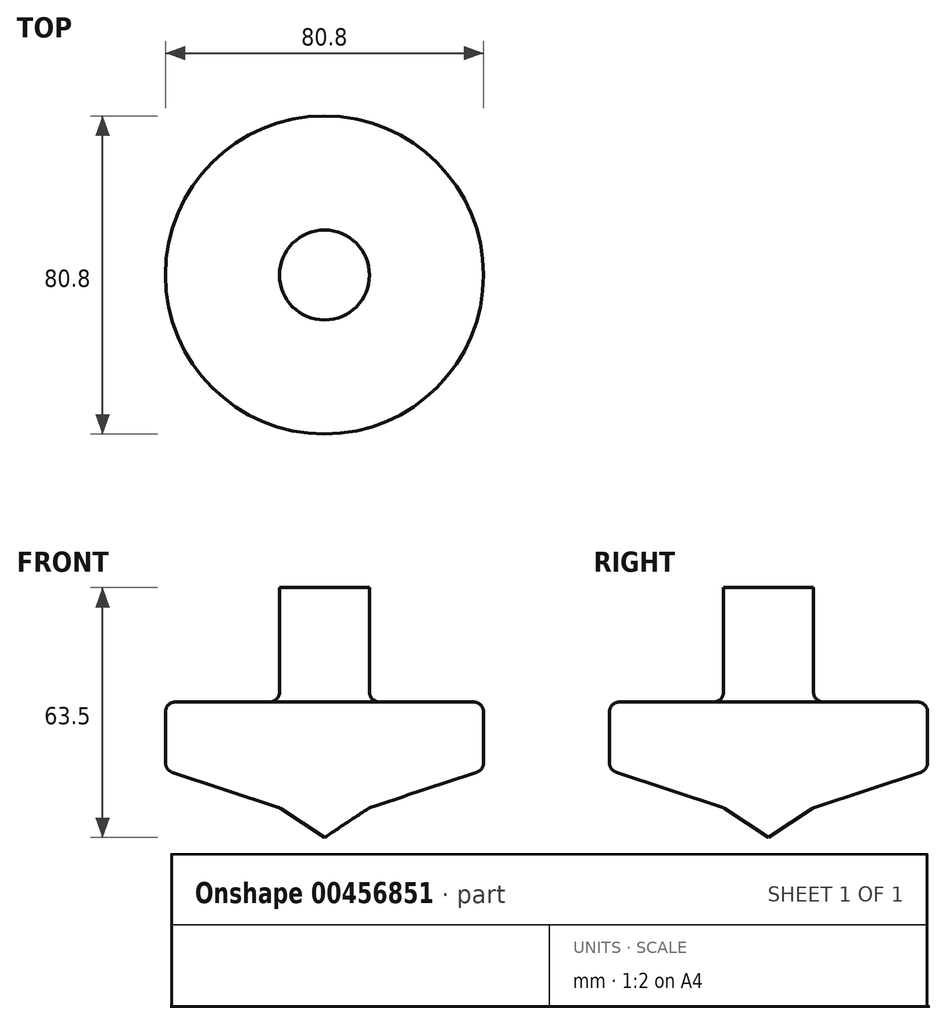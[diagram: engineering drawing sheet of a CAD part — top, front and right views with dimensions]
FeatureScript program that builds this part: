
annotation { "Feature Type Name" : "Feature", "Feature Type Description" : "" }
export const myFeature = defineFeature(function(context is Context, id is Id, definition is map)
    precondition{}
    {
        {
            var Q0;
            Q0=qCreatedBy(makeId("Front.planeOp"),FACE);
            var sketch = newSketch(context, id + "F0", { "sketchPlane" : qUnion([Q0])});
            skLineSegment(sketch, "E0", {"start": v(40.4, 18.98) * mm, "end": v(40.4, 31.89) * mm});
            skLineSegment(sketch, "E1", {"start": v(37.86, 34.43) * mm, "end": v(13.97, 34.43) * mm});
            skLineSegment(sketch, "E2", {"start": v(11.43, 36.97) * mm, "end": v(11.43, 63.5) * mm});
            skLineSegment(sketch, "E3", {"start": v(11.43, 63.5) * mm, "end": v(0, 63.5) * mm});
            skLineSegment(sketch, "E4", {"start": v(0, 0) * mm, "end": v(11.15, 7.37) * mm});
            skLineSegment(sketch, "E5", {"start": v(11.75, 7.67) * mm, "end": v(38.66, 16.57) * mm});
            skPoint(sketch, "E6.visualSharp", {"position": v(11.43, 34.43) * mm});
            skArc(sketch, "E6.filletArc", {"start": v(11.43, 36.97) * mm, "mid": v(12.17, 35.17) * mm, "end": v(13.97, 34.43) * mm});
            skPoint(sketch, "E7.visualSharp", {"position": v(40.4, 34.43) * mm});
            skArc(sketch, "E7.filletArc", {"start": v(40.4, 31.89) * mm, "mid": v(39.66, 33.68) * mm, "end": v(37.86, 34.43) * mm});
            skPoint(sketch, "E8.visualSharp", {"position": v(40.4, 17.14) * mm});
            skArc(sketch, "E8.filletArc", {"start": v(38.66, 16.57) * mm, "mid": v(39.92, 17.5) * mm, "end": v(40.4, 18.98) * mm});
            skPoint(sketch, "E9.visualSharp", {"position": v(11.43, 7.56) * mm});
            skArc(sketch, "E9.filletArc", {"start": v(11.75, 7.67) * mm, "mid": v(11.44, 7.54) * mm, "end": v(11.15, 7.37) * mm});
            skLineSegment(sketch, "E10", {"start": v(0, 63.5) * mm, "end": v(0, 0) * mm});
            skSolve(sketch);
        }
        {
            var Q0;
            Q0=makeQuery(id+"F0.imprint","IMPRINT",FACE,{"disambiguationData":[TD([[makeQuery(id+"F0.imprint","IMPRINT",EDGE,{"derivedFrom":sQuery(id+"F0.wireOp",EDGE,"E0")}),1.0]])]});
            var Q1;
            Q1=sQuery(id+"F0.wireOp",EDGE,"E10");
            revolve(context, id + "F1", {"entities" : qUnion([Q0]), "axis" : qUnion([Q1]), "revolveType" : RevolveType.FULL});
        }
    });
